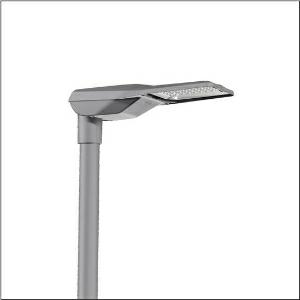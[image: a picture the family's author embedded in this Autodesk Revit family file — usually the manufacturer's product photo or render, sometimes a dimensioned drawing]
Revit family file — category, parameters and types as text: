
# Revit family: streetlight_sl_21_iq_mini___st0_5a_5xe2b41g08hb_4387
name_source: partatom
category: Lighting Fixtures
units: mm (PartAtom-declared; Revit-internal decimal feet)

## family parameters
Cut with Voids When Loaded = No
Host = Face
Light Source = No
Part Type = Normal
Room Calculation Point = No
Round Connector Dimension = Use Diameter
Shared = No

## types (1)
- --- (1 x LED, 9860 lm, 70.9 W, 4000K)
    Apparent Load = 71 VA
    CIE Flux Codes = 41 75 97 100 100
    Color Rendering = 70
    Color Temperature = 4000K
    Default Elevation = 1800 mm
    Description = Streetlight SL 21 mini, mast luminaire, primary light control with lens, of PMMA, primary optical cover: cover, of toughened safety glass, transparent, light distribution: ST0.5a, light emission: direct distribution, primary light characteristic: asymmetric, installation type: post-top, side-entry, LED, High Power LED, rated luminous flux: 9.860lm, luminous efficacy: 139lm/W, light colour: 740, colour temperature: 4000K, control gear: ECG iQ, control: Street-Remote, Auto-Match, Temp-Guard, Lumen-Switch, Night-Set, Smart-Wire, Light-Fading, Desk-Remote (wireless, voltage-free reading and setting of iQ features in the workshop via application-optimized NFC function/RFID function), optimised constant luminous flux control (CLO 2.0), mains connection: 220..240V, AC, 50/60Hz, start of lifetime: 71W, end of lifetime: 75W, reduction: 31W, luminaire housing, of diecast aluminium, powder-coated, Siteco® metallic grey (DB 702S), corrosivity category C5 according to DIN EN ISO 12944, length: 628mm, width: 235mm, height: 110mm, spigot size: 60/76mm (post-top) and 42/60/76mm (side-entry), mast flange for spigot size: 42mm: 5XC10008XM4, 60mm: 5XC10008XM2, 76/60mm: 5XC10108XM1, protection rating (complete): IP66, insulation class (complete): insulation class II (safety insulation), certification: CE, ENEC, VDE, impact resistance: IK09, permissible operating ambient temperature for outdoor applications: -40..+50°C, standard-compliant lighting for roads and squares, packaging unit: 1 piece

Light Distribution: ST0.5a
    Height = 110 mm
    Lamp = 1 x LED
    Lamp Light Flux = 9860 lm
    Lamp Power = 70.9 W
    Lamp count = 1
    Length = 625 mm
    Luminous efficacy = 139 lm/W
    Manufacturer = Siteco
    ModVariant = No
    Model = 5XE2B41G08HB
    Number of Poles = 1
    OnlyDefault = Yes
    Power Factor = 1
    Product Name = Streetlight SL 21 iQ mini | ST0.5a
    Product group = mast luminaire | pylon top
    ProductGroupID = 6100
    Protection Class = Protection class II
    Protection Degree = IP 66
    RLX_Detail_Level = 1
    RlxData = <blob elided: 103313 chars, md5=4480d4cb>
    Socket = socket
    Standby Power = 0 W
    System Light Flux = 9860 lm
    System Power = 71 W
    Type Comments = factory setting: luminous flux: 100 % | dim-lin: 254 | 711 mA
    Type Image = l_1003519.jpg
    URL = http://relux.com
    VarID = @adj_069759
    Voltage = 0 V
    Weight = 0.00 kg
    Width = 234 mm

## geometry (parser evidence)
native form markers: Blend x4, Sweep x10
no freeform markers — native parametric forms only
